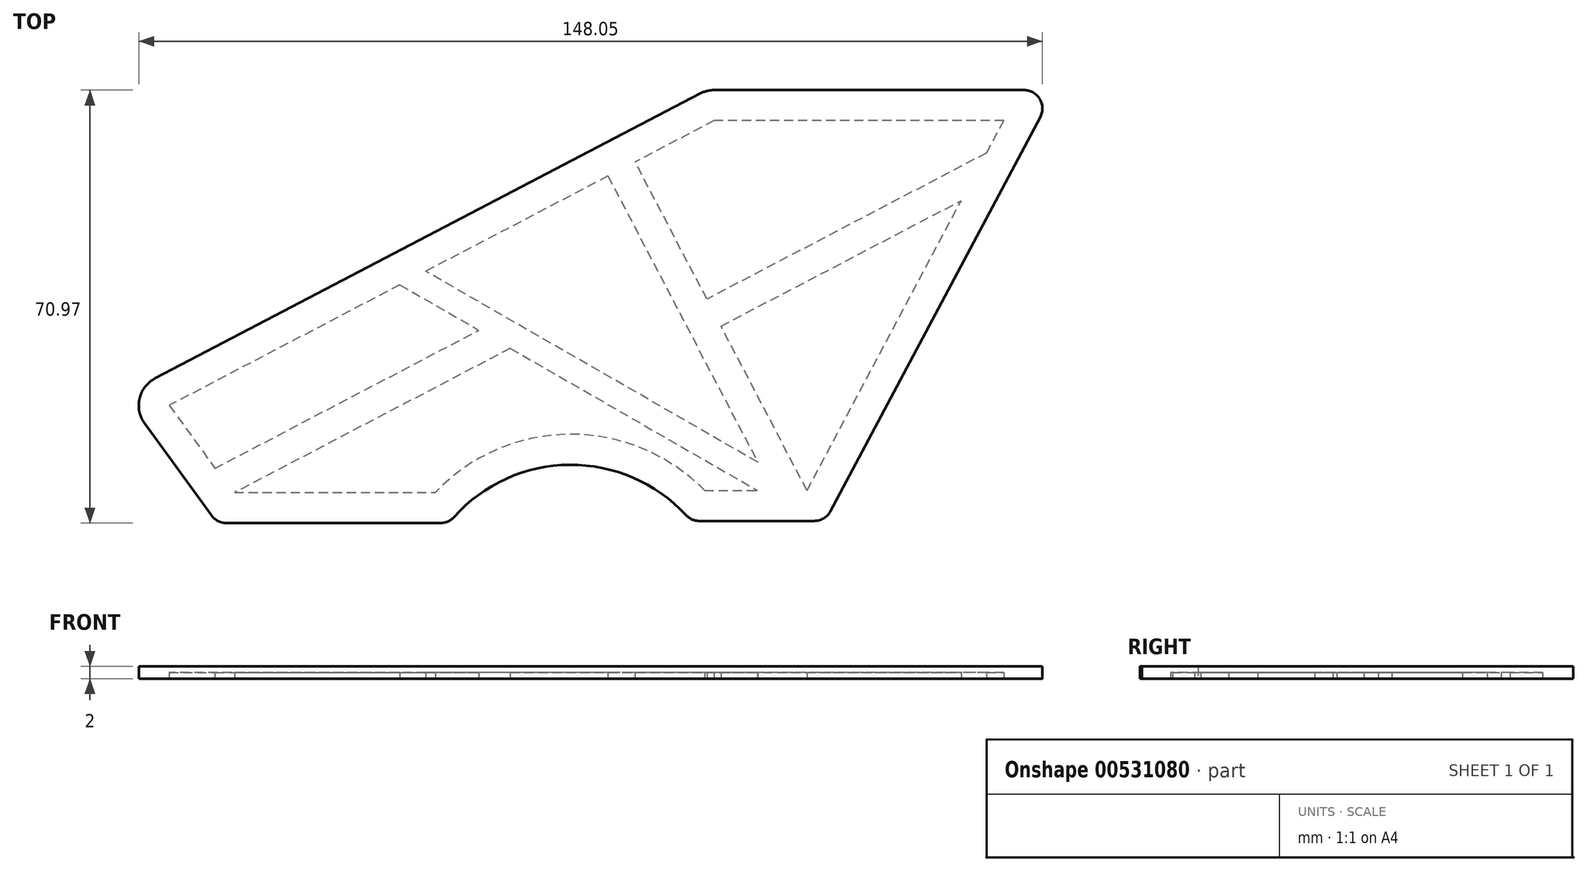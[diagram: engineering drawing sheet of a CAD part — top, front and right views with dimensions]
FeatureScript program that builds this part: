
annotation { "Feature Type Name" : "Feature", "Feature Type Description" : "" }
export const myFeature = defineFeature(function(context is Context, id is Id, definition is map)
    precondition{}
    {
        {
            var Q0;
            Q0=qCreatedBy(makeId("Top.planeOp"),FACE);
            var sketch = newSketch(context, id + "F0", { "sketchPlane" : qUnion([Q0])});
            skLineSegment(sketch, "E0", {"start": v(3.4, -4.69) * mm, "end": v(14.38, -19.8) * mm});
            skLineSegment(sketch, "E1", {"start": v(16.81, -21.03) * mm, "end": v(51.9, -21.03) * mm});
            skLineSegment(sketch, "E2", {"start": v(94.3, -20.7) * mm, "end": v(113.13, -20.7) * mm});
            skLineSegment(sketch, "E3", {"start": v(115.78, -19.1) * mm, "end": v(150.15, 45.53) * mm});
            skLineSegment(sketch, "E4", {"start": v(147.5, 49.94) * mm, "end": v(96.72, 49.94) * mm});
            skLineSegment(sketch, "E5", {"start": v(94.4, 49.37) * mm, "end": v(5.13, 2.68) * mm});
            skArc(sketch, "E6", {"start": v(92.09, -19.73) * mm, "mid": v(73.04, -11.49) * mm, "end": v(54.13, -20.04) * mm});
            skLineSegment(sketch, "E7.0", {"start": v(96.72, 44.94) * mm, "end": v(7.45, -1.75) * mm});
            skLineSegment(sketch, "E7.1", {"start": v(144.17, 44.94) * mm, "end": v(96.72, 44.94) * mm});
            skLineSegment(sketch, "E7.2", {"start": v(17.83, -16.03) * mm, "end": v(51.02, -16.03) * mm});
            skArc(sketch, "E7.3", {"start": v(95.15, -15.7) * mm, "mid": v(73.01, -6.49) * mm, "end": v(51.02, -16.03) * mm});
            skLineSegment(sketch, "E7.4", {"start": v(95.15, -15.7) * mm, "end": v(111.93, -15.7) * mm});
            skLineSegment(sketch, "E7.5", {"start": v(7.45, -1.75) * mm, "end": v(17.83, -16.03) * mm});
            skLineSegment(sketch, "E7.6", {"start": v(111.93, -15.7) * mm, "end": v(144.17, 44.94) * mm});
            skLineSegment(sketch, "E8", {"start": v(111.93, -15.7) * mm, "end": v(97.85, 11.24) * mm});
            skLineSegment(sketch, "E9", {"start": v(83.76, 38.17) * mm, "end": v(79.33, 35.85) * mm});
            skLineSegment(sketch, "E10", {"start": v(79.33, 35.85) * mm, "end": v(103.86, -11.05) * mm});
            skPoint(sketch, "E10.endSnap0", {"position": v(103.54, -15.7) * mm});
            skLineSegment(sketch, "E11", {"start": v(103.86, -11.05) * mm, "end": v(49.48, 20.23) * mm});
            skLineSegment(sketch, "E12", {"start": v(49.48, 20.23) * mm, "end": v(45.22, 18) * mm});
            skLineSegment(sketch, "E13", {"start": v(45.22, 18) * mm, "end": v(58.18, 10.55) * mm});
            skLineSegment(sketch, "E14", {"start": v(97.85, 11.24) * mm, "end": v(137.2, 31.81) * mm});
            skLineSegment(sketch, "E15", {"start": v(141.35, 39.63) * mm, "end": v(95.53, 15.67) * mm});
            skLineSegment(sketch, "E16", {"start": v(14.94, -12.06) * mm, "end": v(58.18, 10.55) * mm});
            skLineSegment(sketch, "E17", {"start": v(63.32, 7.6) * mm, "end": v(18.13, -16.03) * mm});
            skLineSegment(sketch, "E18.trimOffspring", {"start": v(63.32, 7.6) * mm, "end": v(103.81, -15.7) * mm});
            skLineSegment(sketch, "E19.trimOffspring", {"start": v(95.53, 15.67) * mm, "end": v(83.76, 38.17) * mm});
            skPoint(sketch, "E20.orphan", {"position": v(106.29, -15.7) * mm});
            skPoint(sketch, "E21.visualSharp", {"position": v(0, 0) * mm});
            skArc(sketch, "E21.filletArc", {"start": v(5.13, 2.68) * mm, "mid": v(2.58, -0.6) * mm, "end": v(3.4, -4.69) * mm});
            skPoint(sketch, "E22.visualSharp", {"position": v(152.5, 49.94) * mm});
            skArc(sketch, "E22.filletArc", {"start": v(150.15, 45.53) * mm, "mid": v(150.07, 48.49) * mm, "end": v(147.5, 49.94) * mm});
            skPoint(sketch, "E23.visualSharp", {"position": v(95.5, 49.94) * mm});
            skArc(sketch, "E23.filletArc", {"start": v(96.72, 49.94) * mm, "mid": v(95.53, 49.8) * mm, "end": v(94.4, 49.37) * mm});
            skPoint(sketch, "E24.visualSharp", {"position": v(114.94, -20.7) * mm});
            skArc(sketch, "E24.filletArc", {"start": v(113.13, -20.7) * mm, "mid": v(114.68, -20.26) * mm, "end": v(115.78, -19.1) * mm});
            skPoint(sketch, "E25.visualSharp", {"position": v(15.28, -21.03) * mm});
            skArc(sketch, "E25.filletArc", {"start": v(14.38, -19.8) * mm, "mid": v(15.45, -20.7) * mm, "end": v(16.81, -21.03) * mm});
            skPoint(sketch, "E26.visualSharp", {"position": v(53.28, -21.03) * mm});
            skArc(sketch, "E26.filletArc", {"start": v(51.9, -21.03) * mm, "mid": v(53.12, -20.77) * mm, "end": v(54.13, -20.04) * mm});
            skPoint(sketch, "E27.visualSharp", {"position": v(92.94, -20.7) * mm});
            skArc(sketch, "E27.filletArc", {"start": v(92.09, -19.73) * mm, "mid": v(93.09, -20.44) * mm, "end": v(94.3, -20.7) * mm});
            skSolve(sketch);
        }
        {
            var Q0;
            Q0=makeQuery(id+"F0.imprint","IMPRINT",FACE,{"disambiguationData":[TD([[makeQuery(id+"F0.imprint","IMPRINT",EDGE,{"derivedFrom":sQuery(id+"F0.wireOp",EDGE,"E0")}),1.0]])]});
            var Q1;
            Q1=makeQuery(id+"F0.imprint","IMPRINT",FACE,{"disambiguationData":[TD([[makeQuery(id+"F0.imprint","IMPRINT",EDGE,{"derivedFrom":sQuery(id+"F0.wireOp",EDGE,"E7.0")}),1.0]])]});
            var Q2;
            {var subQ0=sQuery(id+"F0.wireOp",EDGE,"E12");Q2=makeQuery(id+"F0.imprint","IMPRINT",FACE,{"disambiguationData":[TD([[makeQuery(id+"F0.imprint","IMPRINT",EDGE,{"derivedFrom":subQ0}),1.0]])]});}
            var Q3;
            {var subQ0=sQuery(id+"F0.wireOp",EDGE,"E8");Q3=makeQuery(id+"F0.imprint","IMPRINT",FACE,{"disambiguationData":[TD([[makeQuery(id+"F0.imprint","IMPRINT",EDGE,{"derivedFrom":subQ0}),1.0]])]});}
            var Q4;
            {var subQ1=sQuery(id+"F0.wireOp",EDGE,"E7.4");var subQ3=sQuery(id+"F0.wireOp",EDGE,"E10");var subQ4=makeQuery(id+"F0.imprint","INTERSECT",VERTEX,{"derivedFrom":[subQ1,subQ3]});Q4=makeQuery(id+"F0.imprint","IMPRINT",FACE,{"disambiguationData":[TD([[makeQuery(id+"F0.imprint","IMPRINT",EDGE,{"disambiguationData":[TD([[subQ4,1.0]])],"derivedFrom":subQ3}),1.0]])]});}
            var Q5;
            Q5=makeQuery(id+"F0.imprint","IMPRINT",FACE,{"disambiguationData":[TD([[makeQuery(id+"F0.imprint","IMPRINT",EDGE,{"derivedFrom":sQuery(id+"F0.wireOp",EDGE,"E7.2")}),1.0]])]});
            var Q6;
            {var subQ0=sQuery(id+"F0.wireOp",EDGE,"E7.1");Q6=makeQuery(id+"F0.imprint","IMPRINT",FACE,{"disambiguationData":[TD([[makeQuery(id+"F0.imprint","IMPRINT",EDGE,{"derivedFrom":subQ0}),1.0]])]});}
            var Q7;
            {var subQ3=sQuery(id+"F0.wireOp",EDGE,"E13");Q7=makeQuery(id+"F0.imprint","IMPRINT",FACE,{"disambiguationData":[TD([[makeQuery(id+"F0.imprint","IMPRINT",EDGE,{"derivedFrom":subQ3}),-1.0]])]});}
            var Q8;
            {var subQ0=sQuery(id+"F0.wireOp",EDGE,"E8");Q8=makeQuery(id+"F0.imprint","IMPRINT",FACE,{"disambiguationData":[TD([[makeQuery(id+"F0.imprint","IMPRINT",EDGE,{"derivedFrom":subQ0}),-1.0]])]});}
            extrude(context, id + "F1", {"entities" : qUnion([Q0, Q1, Q2, Q3, Q4, Q5, Q6, Q7, Q8]), "depth" : 2 * mm, "offsetDistance" : 25 * mm});
        }
        {
            var Q0;
            Q0=makeQuery(id+"F0.imprint","IMPRINT",FACE,{"disambiguationData":[TD([[makeQuery(id+"F0.imprint","IMPRINT",EDGE,{"derivedFrom":sQuery(id+"F0.wireOp",EDGE,"E7.0")}),1.0]])]});
            var Q1;
            {var subQ0=sQuery(id+"F0.wireOp",EDGE,"E7.1");Q1=makeQuery(id+"F0.imprint","IMPRINT",FACE,{"disambiguationData":[TD([[makeQuery(id+"F0.imprint","IMPRINT",EDGE,{"derivedFrom":subQ0}),1.0]])]});}
            var Q2;
            Q2=makeQuery(id+"F0.imprint","IMPRINT",FACE,{"disambiguationData":[TD([[makeQuery(id+"F0.imprint","IMPRINT",EDGE,{"derivedFrom":sQuery(id+"F0.wireOp",EDGE,"E7.2")}),1.0]])]});
            var Q3;
            {var subQ0=sQuery(id+"F0.wireOp",EDGE,"E8");Q3=makeQuery(id+"F0.imprint","IMPRINT",FACE,{"disambiguationData":[TD([[makeQuery(id+"F0.imprint","IMPRINT",EDGE,{"derivedFrom":subQ0}),-1.0]])]});}
            var Q4;
            {var subQ3=sQuery(id+"F0.wireOp",EDGE,"E13");Q4=makeQuery(id+"F0.imprint","IMPRINT",FACE,{"disambiguationData":[TD([[makeQuery(id+"F0.imprint","IMPRINT",EDGE,{"derivedFrom":subQ3}),-1.0]])]});}
            extrude(context, id + "F2", {"entities" : qUnion([Q0, Q1, Q2, Q3, Q4]), "operationType" : NewBodyOperationType.REMOVE, "depth" : 1 * mm, "offsetDistance" : 25 * mm});
        }
    });
